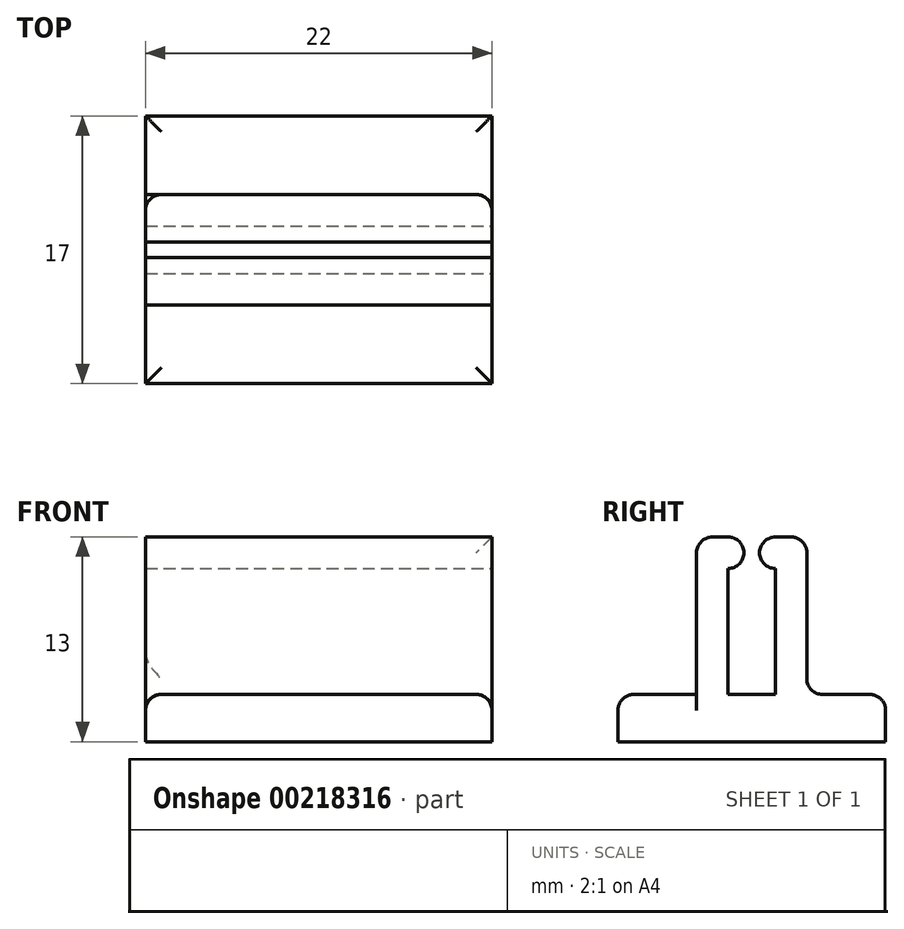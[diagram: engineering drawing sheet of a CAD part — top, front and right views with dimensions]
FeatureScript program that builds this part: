
annotation { "Feature Type Name" : "Feature", "Feature Type Description" : "" }
export const myFeature = defineFeature(function(context is Context, id is Id, definition is map)
    precondition{}
    {
        {
            var Q0;
            Q0=qCreatedBy(makeId("Top.planeOp"),FACE);
            var sketch = newSketch(context, id + "F0", { "sketchPlane" : qUnion([Q0])});
            skLineSegment(sketch, "E0.bottom", {"start": v(11, -8.5) * mm, "end": v(-11, -8.5) * mm});
            skLineSegment(sketch, "E0.top", {"start": v(11, 8.5) * mm, "end": v(-11, 8.5) * mm});
            skLineSegment(sketch, "E0.left", {"start": v(11, -8.5) * mm, "end": v(11, 8.5) * mm});
            skLineSegment(sketch, "E0.right", {"start": v(-11, -8.5) * mm, "end": v(-11, 8.5) * mm});
            skPoint(sketch, "E0.middle", {"position": v(0, 0) * mm});
            skSolve(sketch);
        }
        {
            var Q0;
            Q0 = qSketchRegion(id + "F0", true);
            extrude(context, id + "F1", {"entities" : qUnion([Q0]), "depth" : 3 * mm, "offsetDistance" : 25 * mm});
        }
        {
            var Q0;
            Q0=makeQuery(id+"F1.opExtrude","CAP_FACE",FACE,{"disambiguationData":[OSD([sQuery(id+"F0.wireOp",EDGE,"E0.bottom"),sQuery(id+"F0.wireOp",EDGE,"E0.top"),sQuery(id+"F0.wireOp",EDGE,"E0.left"),sQuery(id+"F0.wireOp",EDGE,"E0.right")])],"isStart":false});
            var sketch = newSketch(context, id + "F2", { "sketchPlane" : qUnion([Q0])});
            skLineSegment(sketch, "E1", {"start": v(-18.53, 0) * mm, "end": v(21.47, 0) * mm, "construction": true});
            skLineSegment(sketch, "E2.bottom", {"start": v(-11, 3.5) * mm, "end": v(11, 3.5) * mm});
            skLineSegment(sketch, "E2.top", {"start": v(-11, 1.5) * mm, "end": v(11, 1.5) * mm});
            skLineSegment(sketch, "E2.left", {"start": v(-11, 3.5) * mm, "end": v(-11, 1.5) * mm});
            skLineSegment(sketch, "E2.right", {"start": v(11, 3.5) * mm, "end": v(11, 1.5) * mm});
            skLineSegment(sketch, "E3.MirrorCS", {"start": v(-11, -1.5) * mm, "end": v(11, -1.5) * mm});
            skLineSegment(sketch, "E4.MirrorCS", {"start": v(-11, -3.5) * mm, "end": v(11, -3.5) * mm});
            skLineSegment(sketch, "E5.MirrorCS", {"start": v(-11, -3.5) * mm, "end": v(-11, -1.5) * mm});
            skLineSegment(sketch, "E6.MirrorCS", {"start": v(11, -3.5) * mm, "end": v(11, -1.5) * mm});
            skSolve(sketch);
        }
        {
            var Q0;
            Q0 = qSketchRegion(id + "F2", true);
            extrude(context, id + "F3", {"entities" : qUnion([Q0]), "operationType" : NewBodyOperationType.ADD, "depth" : 10 * mm, "offsetDistance" : 25 * mm});
        }
        {
            var Q0;
            Q0=makeQuery(id+"F3.opExtrude","SWEPT_FACE",FACE,{"disambiguationData":[OSD([sQuery(id+"F2.wireOp",EDGE,"E2.top")])]});
            var sketch = newSketch(context, id + "F4", { "sketchPlane" : qUnion([Q0])});
            skLineSegment(sketch, "E7.bottom", {"start": v(11, 13) * mm, "end": v(-11, 13) * mm});
            skLineSegment(sketch, "E7.top", {"start": v(11, 12) * mm, "end": v(-11, 12) * mm});
            skLineSegment(sketch, "E7.left", {"start": v(11, 13) * mm, "end": v(11, 12) * mm});
            skLineSegment(sketch, "E7.right", {"start": v(-11, 13) * mm, "end": v(-11, 12) * mm});
            skSolve(sketch);
        }
        {
            var Q0;
            Q0 = qSketchRegion(id + "F4", true);
            var Q1;
            Q1=sQuery(id+"F4.wireOp",EDGE,"E7.top");
            revolve(context, id + "F5", {"operationType" : NewBodyOperationType.ADD, "surfaceOperationType" : NewSurfaceOperationType.NEW, "entities" : qUnion([Q0]), "axis" : qUnion([Q1]), "revolveType" : RevolveType.FULL});
        }
        {
            var Q0;
            Q0=makeQuery(id+"F1.opExtrude","SWEPT_BODY",BODY,{"disambiguationData":[OSD([sQuery(id+"F0.wireOp",EDGE,"E0.bottom"),sQuery(id+"F0.wireOp",EDGE,"E0.top"),sQuery(id+"F0.wireOp",EDGE,"E0.left"),sQuery(id+"F0.wireOp",EDGE,"E0.right")])]});
            var Q1;
            Q1=qCreatedBy(makeId("Front.planeOp"),FACE);
            mirror(context, id + "F6", {"operationType" : NewBodyOperationType.ADD, "entities" : qUnion([Q0]), "mirrorPlane" : qUnion([Q1])});
        }
        {
            var Q0;
            Q0=makeQuery(id+"F3.opExtrude","CAP_EDGE",EDGE,{"disambiguationData":[OSD([sQuery(id+"F2.wireOp",EDGE,"E4.MirrorCS")])],"isStart":true});
            var Q1;
            Q1=makeQuery(id+"F3.opExtrude","CAP_EDGE",EDGE,{"disambiguationData":[OSD([sQuery(id+"F2.wireOp",EDGE,"E4.MirrorCS")])],"isStart":false});
            var Q2;
            Q2=makeQuery(id+"F3.opExtrude","SWEPT_EDGE",EDGE,{"disambiguationData":[OSD([sQuery(id+"F0.wireOp",EDGE,"E0.left"),sQuery(id+"F2.wireOp",EDGE,"E2.bottom"),sQuery(id+"F2.wireOp",EDGE,"E2.right")])]});
            var Q3;
            {var subQ0=sQuery(id+"F0.wireOp",EDGE,"E0.left");var subQ1=sQuery(id+"F0.wireOp",EDGE,"E0.bottom");Q3=makeQuery(id+"F3.boolean.opBoolean","SPLIT",EDGE,{"disambiguationData":[TD([makeQuery(id+"F1.opExtrude","SWEPT_FACE",FACE,{"disambiguationData":[OSD([subQ1])]})])],"derivedFrom":makeQuery(id+"F1.opExtrude","CAP_EDGE",EDGE,{"disambiguationData":[OSD([subQ0])],"isStart":false})});}
            var Q4;
            Q4=makeQuery(id+"F1.opExtrude","CAP_EDGE",EDGE,{"disambiguationData":[OSD([sQuery(id+"F0.wireOp",EDGE,"E0.bottom")])],"isStart":false});
            var Q5;
            {var subQ0=sQuery(id+"F0.wireOp",EDGE,"E0.right");var subQ1=sQuery(id+"F0.wireOp",EDGE,"E0.bottom");Q5=makeQuery(id+"F3.boolean.opBoolean","SPLIT",EDGE,{"disambiguationData":[TD([makeQuery(id+"F1.opExtrude","SWEPT_FACE",FACE,{"disambiguationData":[OSD([subQ1])]})])],"derivedFrom":makeQuery(id+"F1.opExtrude","CAP_EDGE",EDGE,{"disambiguationData":[OSD([subQ0])],"isStart":false})});}
            var Q6;
            Q6=makeQuery(id+"F3.opExtrude","CAP_EDGE",EDGE,{"disambiguationData":[OSD([sQuery(id+"F2.wireOp",EDGE,"E2.bottom")])],"isStart":false});
            var Q7;
            Q7=makeQuery(id+"F3.opExtrude","CAP_EDGE",EDGE,{"disambiguationData":[OSD([sQuery(id+"F2.wireOp",EDGE,"E2.bottom")])],"isStart":true});
            var Q8;
            {var subQ0=sQuery(id+"F0.wireOp",EDGE,"E0.right");var subQ1=sQuery(id+"F0.wireOp",EDGE,"E0.top");Q8=makeQuery(id+"F3.boolean.opBoolean","SPLIT",EDGE,{"disambiguationData":[TD([makeQuery(id+"F1.opExtrude","SWEPT_FACE",FACE,{"disambiguationData":[OSD([subQ1])]})])],"derivedFrom":makeQuery(id+"F1.opExtrude","CAP_EDGE",EDGE,{"disambiguationData":[OSD([subQ0])],"isStart":false})});}
            var Q9;
            {var subQ0=sQuery(id+"F0.wireOp",EDGE,"E0.left");var subQ1=sQuery(id+"F0.wireOp",EDGE,"E0.top");Q9=makeQuery(id+"F3.boolean.opBoolean","SPLIT",EDGE,{"disambiguationData":[TD([makeQuery(id+"F1.opExtrude","SWEPT_FACE",FACE,{"disambiguationData":[OSD([subQ1])]})])],"derivedFrom":makeQuery(id+"F1.opExtrude","CAP_EDGE",EDGE,{"disambiguationData":[OSD([subQ0])],"isStart":false})});}
            var Q10;
            Q10=makeQuery(id+"F1.opExtrude","CAP_EDGE",EDGE,{"disambiguationData":[OSD([sQuery(id+"F0.wireOp",EDGE,"E0.top")])],"isStart":false});
            fillet(context, id + "F7", {"entities" : qUnion([Q0, Q1, Q2, Q3, Q4, Q5, Q6, Q7, Q8, Q9, Q10]), "radius" : 1 * mm, "tangentPropagation" : true, "allowEdgeOverflow" : false});
        }
    });
